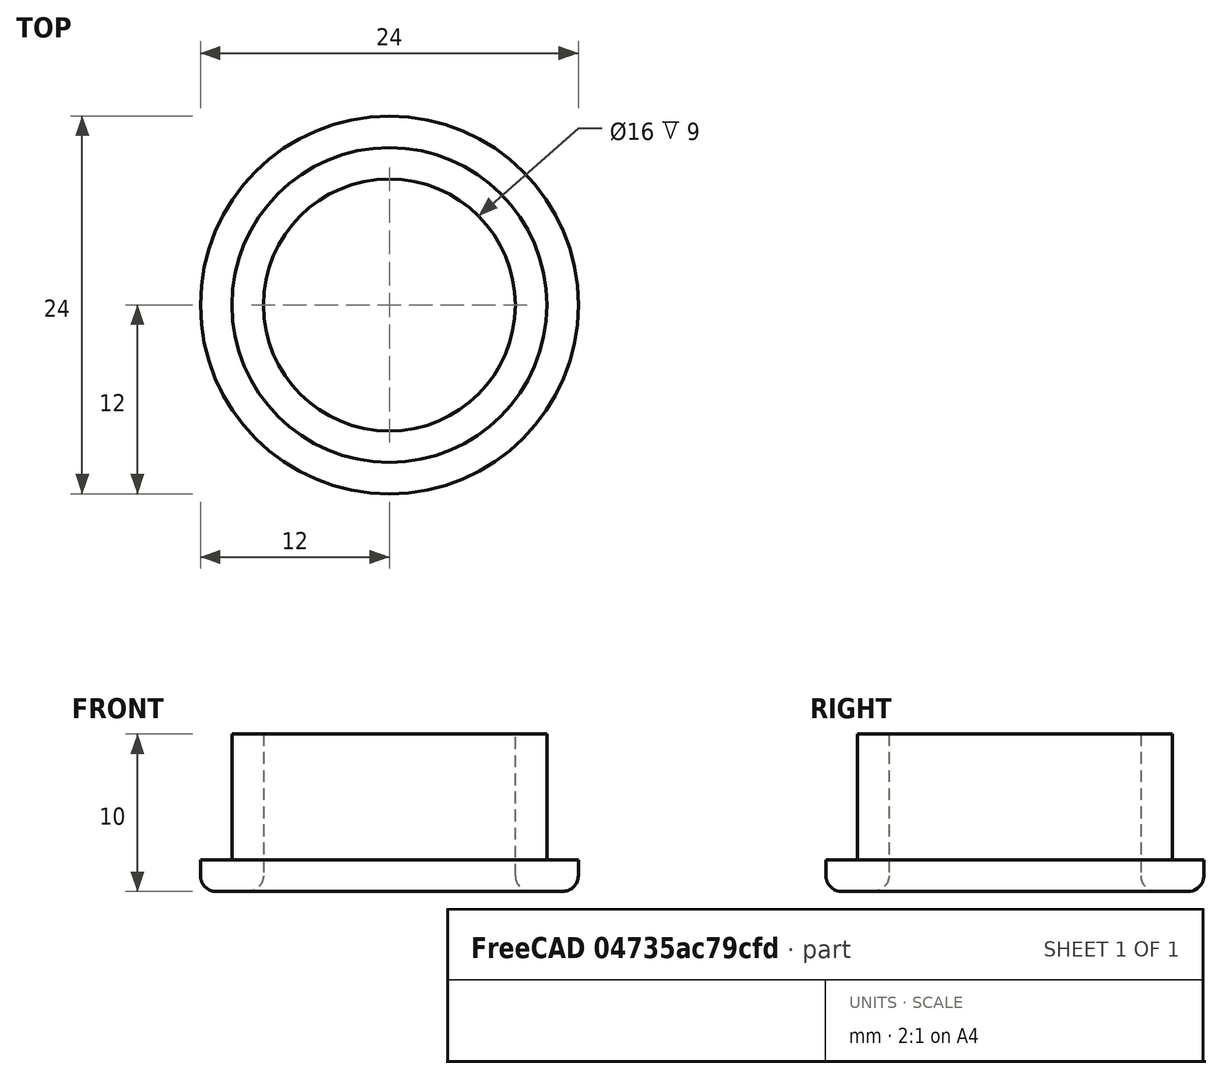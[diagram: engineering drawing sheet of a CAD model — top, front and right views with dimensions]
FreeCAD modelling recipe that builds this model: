
FCSTD DOCUMENT  (FreeCAD 1.0R39109 (Git))
Label: LowPowerBushing
License: All rights reserved
LicenseURL: https://en.wikipedia.org/wiki/All_rights_reserved
objects: Part::Cylinder×3, Part::MultiFuse×1, Part::Cut×1, Part::Fillet×1
note: 6 computed .brp shape members not serialized (recipe doc carries the construction recipe); baked Part::Feature solids carry a one-line shape summary decoded from their .brp

FEATURE [Part::Cylinder] Cylinder
  Angle = 360
  AttacherType = Attacher::AttachEngine3D
  FirstAngle = 0
  Height = 10
  Radius = 8
  SecondAngle = 0
FEATURE [Part::Cylinder] Cylinder001
  Angle = 360
  AttacherType = Attacher::AttachEngine3D
  FirstAngle = 0
  Height = 2
  Radius = 12
  SecondAngle = 0
FEATURE [Part::Cylinder] Cylinder002
  Angle = 360
  AttacherType = Attacher::AttachEngine3D
  FirstAngle = 0
  Height = 8
  Placement = pos=(0,0,2) rot=(0,0,1;0rad)
  Radius = 10
  SecondAngle = 0
FEATURE [Part::MultiFuse] Fusion
  Shapes = -> [Cylinder002,Cylinder001]
FEATURE [Part::Cut] Cut
  Base = -> Fusion
  Tool = -> Cylinder
FEATURE [Part::Fillet] Fillet
  Base = -> Cut
  EdgeLinks = -> Cut [Edge7,Edge9]
  Edges = 2 edges r=1: [Edge7,Edge9]
